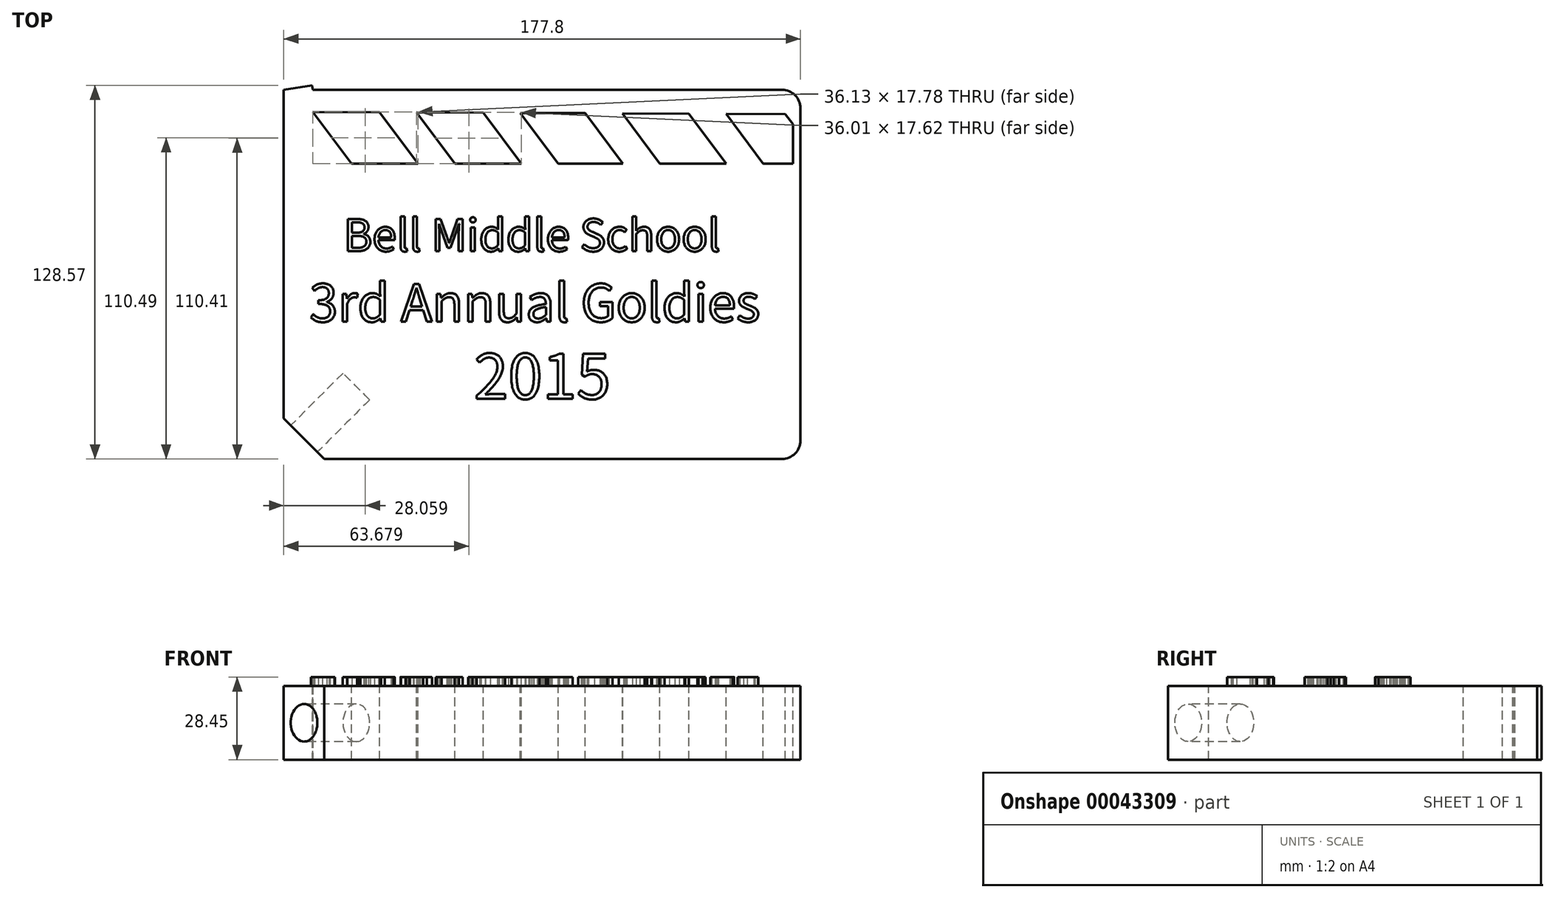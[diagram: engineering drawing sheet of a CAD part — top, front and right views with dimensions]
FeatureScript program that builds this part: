
annotation { "Feature Type Name" : "Feature", "Feature Type Description" : "" }
export const myFeature = defineFeature(function(context is Context, id is Id, definition is map)
    precondition{}
    {
        {
            var Q0;
            Q0=qCreatedBy(makeId("Top.planeOp"),FACE);
            var sketch = newSketch(context, id + "F0", { "sketchPlane" : qUnion([Q0])});
            skLineSegment(sketch, "E0.bottom", {"start": v(-85.65, 77.21) * mm, "end": v(85.8, 77.21) * mm});
            skLineSegment(sketch, "E0.top", {"start": v(-79.3, -49.79) * mm, "end": v(85.8, -49.79) * mm});
            skLineSegment(sketch, "E0.left", {"start": v(-85.65, 77.21) * mm, "end": v(-85.65, -43.44) * mm});
            skLineSegment(sketch, "E0.right", {"start": v(92.15, 70.86) * mm, "end": v(92.15, -43.44) * mm});
            skLineSegment(sketch, "E1", {"start": v(-85.65, 77.21) * mm, "end": v(-108.44, 107.74) * mm});
            skLineSegment(sketch, "E2", {"start": v(-102.2, 99.38) * mm, "end": v(-85.65, 77.21) * mm});
            skLineSegment(sketch, "E3", {"start": v(-85.65, 77.21) * mm, "end": v(79.18, 103.64) * mm});
            skLineSegment(sketch, "E4", {"start": v(83.36, 113.58) * mm, "end": v(69.28, 133.5) * mm});
            skLineSegment(sketch, "E5", {"start": v(63.05, 136.1) * mm, "end": v(-98.15, 109.45) * mm});
            skPoint(sketch, "E6.visualSharp", {"position": v(-108.44, 107.74) * mm});
            skArc(sketch, "E6.filletArc", {"start": v(-98.15, 109.45) * mm, "mid": v(-103, 105.55) * mm, "end": v(-102.2, 99.38) * mm});
            skPoint(sketch, "E7.visualSharp", {"position": v(66.98, 136.75) * mm});
            skArc(sketch, "E7.filletArc", {"start": v(69.28, 133.5) * mm, "mid": v(66.54, 135.7) * mm, "end": v(63.05, 136.1) * mm});
            skPoint(sketch, "E8.visualSharp", {"position": v(89.24, 105.25) * mm});
            skArc(sketch, "E8.filletArc", {"start": v(79.18, 103.64) * mm, "mid": v(84.02, 107.45) * mm, "end": v(83.36, 113.58) * mm});
            skPoint(sketch, "E9.visualSharp", {"position": v(92.15, 77.21) * mm});
            skArc(sketch, "E9.filletArc", {"start": v(92.15, 70.86) * mm, "mid": v(90.3, 75.35) * mm, "end": v(85.8, 77.21) * mm});
            skPoint(sketch, "E10.visualSharp", {"position": v(-85.65, -49.79) * mm});
            skArc(sketch, "E10.filletArc", {"start": v(-85.65, -43.44) * mm, "mid": v(-83.79, -47.93) * mm, "end": v(-79.3, -49.79) * mm});
            skPoint(sketch, "E11.visualSharp", {"position": v(92.15, -49.79) * mm});
            skArc(sketch, "E11.filletArc", {"start": v(85.8, -49.79) * mm, "mid": v(90.3, -47.93) * mm, "end": v(92.15, -43.44) * mm});
            skLineSegment(sketch, "E12", {"start": v(70.72, 131.46) * mm, "end": v(83.36, 113.58) * mm});
            skLineSegment(sketch, "E13", {"start": v(-91.83, 85.48) * mm, "end": v(-85.65, 77.21) * mm});
            skLineSegment(sketch, "E14", {"start": v(-74.04, 105.7) * mm, "end": v(-60.84, 88.03) * mm});
            skLineSegment(sketch, "E15", {"start": v(-48.3, 90.04) * mm, "end": v(-61.54, 107.77) * mm});
            skLineSegment(sketch, "E16", {"start": v(-61.54, 107.77) * mm, "end": v(-39.05, 111.5) * mm});
            skLineSegment(sketch, "E17", {"start": v(-39.05, 111.5) * mm, "end": v(-25.73, 93.66) * mm});
            skLineSegment(sketch, "E18", {"start": v(-25.73, 93.66) * mm, "end": v(-25.44, 93.7) * mm});
            skLineSegment(sketch, "E19", {"start": v(-25.44, 93.7) * mm, "end": v(-38.76, 111.54) * mm});
            skLineSegment(sketch, "E20", {"start": v(-27.03, 113.48) * mm, "end": v(-13.67, 95.59) * mm});
            skLineSegment(sketch, "E21", {"start": v(-13.67, 95.59) * mm, "end": v(9.19, 99.25) * mm});
            skLineSegment(sketch, "E22", {"start": v(9.19, 99.25) * mm, "end": v(-4.24, 117.25) * mm});
            skLineSegment(sketch, "E23", {"start": v(8.41, 119.34) * mm, "end": v(21.89, 101.3) * mm});
            skLineSegment(sketch, "E24", {"start": v(21.89, 101.3) * mm, "end": v(44.75, 104.96) * mm});
            skLineSegment(sketch, "E25", {"start": v(44.75, 104.96) * mm, "end": v(31.2, 123.1) * mm});
            skLineSegment(sketch, "E26", {"start": v(43.86, 125.2) * mm, "end": v(57.45, 107) * mm});
            skLineSegment(sketch, "E27", {"start": v(57.45, 107) * mm, "end": v(80.02, 110.61) * mm});
            skLineSegment(sketch, "E28", {"start": v(80.02, 110.61) * mm, "end": v(66.35, 128.92) * mm});
            skLineSegment(sketch, "E29", {"start": v(-74.04, 105.7) * mm, "end": v(-96.9, 101.93) * mm});
            skLineSegment(sketch, "E30", {"start": v(-27.03, 113.48) * mm, "end": v(-4.24, 117.25) * mm});
            skLineSegment(sketch, "E31", {"start": v(8.41, 119.34) * mm, "end": v(31.2, 123.1) * mm});
            skLineSegment(sketch, "E32", {"start": v(43.86, 125.2) * mm, "end": v(66.35, 128.92) * mm});
            skLineSegment(sketch, "E33", {"start": v(-25.44, 93.7) * mm, "end": v(-48.3, 90.04) * mm});
            skLineSegment(sketch, "E34", {"start": v(-60.84, 88.03) * mm, "end": v(-83.78, 84.35) * mm});
            skLineSegment(sketch, "E35", {"start": v(-96.9, 101.93) * mm, "end": v(-83.78, 84.35) * mm});
            skLineSegment(sketch, "E36", {"start": v(-75.87, 78.78) * mm, "end": v(-75.62, 77.21) * mm});
            skSolve(sketch);
        }
        {
            var Q0;
            {var subQ1=sQuery(id+"F0.wireOp",EDGE,"E36");Q0=makeQuery(id+"F0.imprint","IMPRINT",FACE,{"disambiguationData":[TD([[makeQuery(id+"F0.imprint","IMPRINT",EDGE,{"derivedFrom":subQ1}),-1.0]])]});}
            var Q1;
            Q1=makeQuery(id+"F0.imprint","IMPRINT",FACE,{"disambiguationData":[TD([[makeQuery(id+"F0.imprint","IMPRINT",EDGE,{"derivedFrom":sQuery(id+"F0.wireOp",EDGE,"E2")}),1.0]])]});
            var Q2;
            Q2=makeQuery(id+"F0.imprint","IMPRINT",FACE,{"disambiguationData":[TD([[makeQuery(id+"F0.imprint","IMPRINT",EDGE,{"derivedFrom":sQuery(id+"F0.wireOp",EDGE,"E0.top")}),1.0]])]});
            extrude(context, id + "F1", {"entities" : qUnion([Q0, Q1, Q2]), "depth" : 25.4 * mm});
        }
        {
            var Q0;
            Q0=makeQuery(id+"F1.opExtrude","CAP_FACE",FACE,{"disambiguationData":[OSD([sQuery(id+"F0.wireOp",EDGE,"E0.bottom"),sQuery(id+"F0.wireOp",EDGE,"E0.top"),sQuery(id+"F0.wireOp",EDGE,"E0.left"),sQuery(id+"F0.wireOp",EDGE,"E0.right"),sQuery(id+"F0.wireOp",EDGE,"E2"),sQuery(id+"F0.wireOp",EDGE,"E3"),sQuery(id+"F0.wireOp",EDGE,"E4"),sQuery(id+"F0.wireOp",EDGE,"E5"),sQuery(id+"F0.wireOp",EDGE,"E6.filletArc"),sQuery(id+"F0.wireOp",EDGE,"E7.filletArc"),sQuery(id+"F0.wireOp",EDGE,"E8.filletArc"),sQuery(id+"F0.wireOp",EDGE,"E9.filletArc"),sQuery(id+"F0.wireOp",EDGE,"E10.filletArc"),sQuery(id+"F0.wireOp",EDGE,"E11.filletArc"),sQuery(id+"F0.wireOp",EDGE,"E12"),sQuery(id+"F0.wireOp",EDGE,"E13"),sQuery(id+"F0.wireOp",EDGE,"E14"),sQuery(id+"F0.wireOp",EDGE,"E15"),sQuery(id+"F0.wireOp",EDGE,"E16"),sQuery(id+"F0.wireOp",EDGE,"E17"),sQuery(id+"F0.wireOp",EDGE,"E20"),sQuery(id+"F0.wireOp",EDGE,"E21"),sQuery(id+"F0.wireOp",EDGE,"E22"),sQuery(id+"F0.wireOp",EDGE,"E23"),sQuery(id+"F0.wireOp",EDGE,"E24"),sQuery(id+"F0.wireOp",EDGE,"E25"),sQuery(id+"F0.wireOp",EDGE,"E26"),sQuery(id+"F0.wireOp",EDGE,"E27"),sQuery(id+"F0.wireOp",EDGE,"E28"),sQuery(id+"F0.wireOp",EDGE,"E29"),sQuery(id+"F0.wireOp",EDGE,"E30"),sQuery(id+"F0.wireOp",EDGE,"E31"),sQuery(id+"F0.wireOp",EDGE,"E32"),sQuery(id+"F0.wireOp",EDGE,"E33"),sQuery(id+"F0.wireOp",EDGE,"E34"),sQuery(id+"F0.wireOp",EDGE,"E35"),sQuery(id+"F0.wireOp",EDGE,"E36")])],"isStart":false});
            var sketch = newSketch(context, id + "F2", { "sketchPlane" : qUnion([Q0])});
            skPoint(sketch, "E37.endSnap0", {"position": v(-75.74, 78) * mm});
            skLineSegment(sketch, "E38", {"start": v(-75.66, 69.6) * mm, "end": v(-62.39, 51.81) * mm});
            skLineSegment(sketch, "E39", {"start": v(-62.39, 51.81) * mm, "end": v(-39.53, 51.81) * mm});
            skLineSegment(sketch, "E40", {"start": v(-39.53, 51.81) * mm, "end": v(-52.72, 69.49) * mm});
            skLineSegment(sketch, "E41", {"start": v(-39.98, 69.43) * mm, "end": v(-26.83, 51.81) * mm});
            skLineSegment(sketch, "E42", {"start": v(-26.83, 51.81) * mm, "end": v(-3.97, 51.81) * mm});
            skLineSegment(sketch, "E43", {"start": v(-3.97, 51.81) * mm, "end": v(-17.04, 69.33) * mm});
            skLineSegment(sketch, "E44", {"start": v(-4.3, 69.27) * mm, "end": v(8.73, 51.81) * mm});
            skPoint(sketch, "E44.endSnap0", {"position": v(8.2, 51.81) * mm});
            skLineSegment(sketch, "E45", {"start": v(8.73, 51.81) * mm, "end": v(31.06, 51.81) * mm});
            skLineSegment(sketch, "E46", {"start": v(31.06, 51.81) * mm, "end": v(18.1, 69.17) * mm});
            skLineSegment(sketch, "E47", {"start": v(30.85, 69.1) * mm, "end": v(43.76, 51.81) * mm});
            skLineSegment(sketch, "E48", {"start": v(43.76, 51.81) * mm, "end": v(66.62, 51.81) * mm});
            skLineSegment(sketch, "E49", {"start": v(66.62, 51.81) * mm, "end": v(53.79, 69) * mm});
            skLineSegment(sketch, "E50", {"start": v(53.79, 69) * mm, "end": v(54.21, 69) * mm});
            skLineSegment(sketch, "E51", {"start": v(54.21, 69) * mm, "end": v(67.05, 51.81) * mm});
            skLineSegment(sketch, "E52", {"start": v(79.32, 51.81) * mm, "end": v(66.53, 68.95) * mm});
            skLineSegment(sketch, "E53", {"start": v(86.94, 68.86) * mm, "end": v(92.15, 61.88) * mm});
            skLineSegment(sketch, "E54", {"start": v(79.32, 51.81) * mm, "end": v(92.15, 51.81) * mm});
            skLineSegment(sketch, "E55", {"start": v(92.15, 51.81) * mm, "end": v(92.15, 61.88) * mm});
            skLineSegment(sketch, "E56", {"start": v(66.53, 68.95) * mm, "end": v(86.94, 68.86) * mm});
            skLineSegment(sketch, "E57", {"start": v(54.21, 69) * mm, "end": v(30.85, 69.1) * mm});
            skLineSegment(sketch, "E58", {"start": v(18.1, 69.17) * mm, "end": v(-4.3, 69.27) * mm});
            skLineSegment(sketch, "E59", {"start": v(-17.04, 69.33) * mm, "end": v(-39.98, 69.43) * mm});
            skLineSegment(sketch, "E60", {"start": v(-52.72, 69.49) * mm, "end": v(-75.66, 69.6) * mm});
            skLineSegment(sketch, "E61", {"start": v(89.55, 65.37) * mm, "end": v(89.55, 51.81) * mm});
            skSolve(sketch);
        }
        {
            var Q0;
            Q0=makeQuery(id+"F2.imprint","IMPRINT",FACE,{"disambiguationData":[TD([[makeQuery(id+"F2.imprint","IMPRINT",EDGE,{"derivedFrom":sQuery(id+"F2.wireOp",EDGE,"E38")}),1.0]])]});
            var Q1;
            Q1=makeQuery(id+"F2.imprint","IMPRINT",FACE,{"disambiguationData":[TD([[makeQuery(id+"F2.imprint","IMPRINT",EDGE,{"derivedFrom":sQuery(id+"F2.wireOp",EDGE,"E41")}),1.0]])]});
            var Q2;
            Q2=makeQuery(id+"F2.imprint","IMPRINT",FACE,{"disambiguationData":[TD([[makeQuery(id+"F2.imprint","IMPRINT",EDGE,{"derivedFrom":sQuery(id+"F2.wireOp",EDGE,"E44")}),1.0]])]});
            var Q3;
            {var subQ2=sQuery(id+"F2.wireOp",EDGE,"E47");Q3=makeQuery(id+"F2.imprint","IMPRINT",FACE,{"disambiguationData":[TD([[makeQuery(id+"F2.imprint","IMPRINT",EDGE,{"derivedFrom":subQ2}),1.0]])]});}
            var Q4;
            Q4=makeQuery(id+"F2.imprint","IMPRINT",FACE,{"disambiguationData":[TD([[makeQuery(id+"F2.imprint","IMPRINT",EDGE,{"derivedFrom":sQuery(id+"F2.wireOp",EDGE,"E52")}),-1.0]])]});
            extrude(context, id + "F3", {"entities" : qUnion([Q0, Q1, Q2, Q3, Q4]), "operationType" : NewBodyOperationType.REMOVE, "endBound" : BoundingType.THROUGH_ALL, "oppositeDirection" : true, "depth" : 25.4 * mm});
        }
        {
            var Q0;
            Q0=makeQuery(id+"F1.opExtrude","CAP_FACE",FACE,{"disambiguationData":[OSD([sQuery(id+"F0.wireOp",EDGE,"E0.bottom"),sQuery(id+"F0.wireOp",EDGE,"E0.top"),sQuery(id+"F0.wireOp",EDGE,"E0.left"),sQuery(id+"F0.wireOp",EDGE,"E0.right"),sQuery(id+"F0.wireOp",EDGE,"E2"),sQuery(id+"F0.wireOp",EDGE,"E3"),sQuery(id+"F0.wireOp",EDGE,"E4"),sQuery(id+"F0.wireOp",EDGE,"E5"),sQuery(id+"F0.wireOp",EDGE,"E6.filletArc"),sQuery(id+"F0.wireOp",EDGE,"E7.filletArc"),sQuery(id+"F0.wireOp",EDGE,"E8.filletArc"),sQuery(id+"F0.wireOp",EDGE,"E9.filletArc"),sQuery(id+"F0.wireOp",EDGE,"E10.filletArc"),sQuery(id+"F0.wireOp",EDGE,"E11.filletArc"),sQuery(id+"F0.wireOp",EDGE,"E12"),sQuery(id+"F0.wireOp",EDGE,"E13"),sQuery(id+"F0.wireOp",EDGE,"E14"),sQuery(id+"F0.wireOp",EDGE,"E15"),sQuery(id+"F0.wireOp",EDGE,"E16"),sQuery(id+"F0.wireOp",EDGE,"E17"),sQuery(id+"F0.wireOp",EDGE,"E20"),sQuery(id+"F0.wireOp",EDGE,"E21"),sQuery(id+"F0.wireOp",EDGE,"E22"),sQuery(id+"F0.wireOp",EDGE,"E23"),sQuery(id+"F0.wireOp",EDGE,"E24"),sQuery(id+"F0.wireOp",EDGE,"E25"),sQuery(id+"F0.wireOp",EDGE,"E26"),sQuery(id+"F0.wireOp",EDGE,"E27"),sQuery(id+"F0.wireOp",EDGE,"E28"),sQuery(id+"F0.wireOp",EDGE,"E29"),sQuery(id+"F0.wireOp",EDGE,"E30"),sQuery(id+"F0.wireOp",EDGE,"E31"),sQuery(id+"F0.wireOp",EDGE,"E32"),sQuery(id+"F0.wireOp",EDGE,"E33"),sQuery(id+"F0.wireOp",EDGE,"E34"),sQuery(id+"F0.wireOp",EDGE,"E35"),sQuery(id+"F0.wireOp",EDGE,"E36")])],"isStart":false});
            var sketch = newSketch(context, id + "F4", { "sketchPlane" : qUnion([Q0])});
            skText(sketch, "E62", { "text": "Bell Middle School", "fontName": "NotoSansCJKjp-Regular.otf"});
            skText(sketch, "E63", { "text": "3rd Annual Goldies", "fontName": "NotoSansCJKjp-Regular.otf"});
            skText(sketch, "E64", { "text": "2015", "fontName": "NotoSansCJKjp-Regular.otf"});
            const initialGuessF4  = {"E62": [-0.0651, 0.02171, 1, 0, 0.01085], "E63": [-0.07686, -0.00254, 1, 0, 0.0127], "E64": [-0.02019, -0.02912, 1, 0, 0.01524]};
            skSetInitialGuess(sketch, initialGuessF4);
            skSolve(sketch);
        }
        {
            var Q0;
            Q0 = qSketchRegion(id + "F4", true);
            extrude(context, id + "F5", {"entities" : qUnion([Q0]), "operationType" : NewBodyOperationType.ADD, "depth" : 3.05 * mm});
        }
        {
            var Q0;
            {var subQ0=sQuery(id+"F0.wireOp",EDGE,"E0.bottom");var subQ1=sQuery(id+"F0.wireOp",EDGE,"E0.top");var subQ2=sQuery(id+"F0.wireOp",EDGE,"E0.left");var subQ3=sQuery(id+"F0.wireOp",EDGE,"E0.right");var subQ4=sQuery(id+"F0.wireOp",EDGE,"E2");var subQ5=sQuery(id+"F0.wireOp",EDGE,"E3");var subQ6=sQuery(id+"F0.wireOp",EDGE,"E4");var subQ7=sQuery(id+"F0.wireOp",EDGE,"E5");var subQ8=sQuery(id+"F0.wireOp",EDGE,"E6.filletArc");var subQ9=sQuery(id+"F0.wireOp",EDGE,"E7.filletArc");var subQ10=sQuery(id+"F0.wireOp",EDGE,"E8.filletArc");var subQ11=sQuery(id+"F0.wireOp",EDGE,"E9.filletArc");var subQ12=sQuery(id+"F0.wireOp",EDGE,"E10.filletArc");var subQ13=sQuery(id+"F0.wireOp",EDGE,"E11.filletArc");var subQ14=sQuery(id+"F0.wireOp",EDGE,"E12");var subQ15=sQuery(id+"F0.wireOp",EDGE,"E13");var subQ16=sQuery(id+"F0.wireOp",EDGE,"E14");var subQ17=sQuery(id+"F0.wireOp",EDGE,"E15");var subQ18=sQuery(id+"F0.wireOp",EDGE,"E16");var subQ19=sQuery(id+"F0.wireOp",EDGE,"E17");var subQ20=sQuery(id+"F0.wireOp",EDGE,"E20");var subQ21=sQuery(id+"F0.wireOp",EDGE,"E21");var subQ22=sQuery(id+"F0.wireOp",EDGE,"E22");var subQ23=sQuery(id+"F0.wireOp",EDGE,"E23");var subQ24=sQuery(id+"F0.wireOp",EDGE,"E24");var subQ25=sQuery(id+"F0.wireOp",EDGE,"E25");var subQ26=sQuery(id+"F0.wireOp",EDGE,"E26");var subQ27=sQuery(id+"F0.wireOp",EDGE,"E27");var subQ28=sQuery(id+"F0.wireOp",EDGE,"E28");var subQ29=sQuery(id+"F0.wireOp",EDGE,"E29");var subQ30=sQuery(id+"F0.wireOp",EDGE,"E30");var subQ31=sQuery(id+"F0.wireOp",EDGE,"E31");var subQ32=sQuery(id+"F0.wireOp",EDGE,"E32");var subQ33=sQuery(id+"F0.wireOp",EDGE,"E33");var subQ34=sQuery(id+"F0.wireOp",EDGE,"E34");var subQ35=sQuery(id+"F0.wireOp",EDGE,"E35");var subQ36=sQuery(id+"F0.wireOp",EDGE,"E36");Q0=makeQuery(id+"F5.boolean.opBoolean","SPLIT",FACE,{"disambiguationData":[TD([makeQuery(id+"F1.opExtrude","SWEPT_FACE",FACE,{"disambiguationData":[OSD([subQ0])]})])],"derivedFrom":makeQuery(id+"F1.opExtrude","CAP_FACE",FACE,{"disambiguationData":[OSD([subQ0,subQ1,subQ2,subQ3,subQ4,subQ5,subQ6,subQ7,subQ8,subQ9,subQ10,subQ11,subQ12,subQ13,subQ14,subQ15,subQ16,subQ17,subQ18,subQ19,subQ20,subQ21,subQ22,subQ23,subQ24,subQ25,subQ26,subQ27,subQ28,subQ29,subQ30,subQ31,subQ32,subQ33,subQ34,subQ35,subQ36])],"isStart":false})});}
            var sketch = newSketch(context, id + "F6", { "sketchPlane" : qUnion([Q0])});
            skLineSegment(sketch, "E65", {"start": v(-85.65, -35.82) * mm, "end": v(-71.68, -49.79) * mm});
            skSolve(sketch);
        }
        {
            var Q0;
            {var subQ1=sQuery(id+"F6.wireOp",EDGE,"E65");Q0=makeQuery(id+"F6.imprint","IMPRINT",FACE,{"disambiguationData":[TD([[makeQuery(id+"F6.imprint","IMPRINT",EDGE,{"derivedFrom":subQ1}),-1.0]])]});}
            extrude(context, id + "F7", {"entities" : qUnion([Q0]), "operationType" : NewBodyOperationType.REMOVE, "endBound" : BoundingType.THROUGH_ALL, "oppositeDirection" : true, "depth" : 25.4 * mm});
        }
        {
            var Q0;
            Q0=makeQuery(id+"F7.boolean.opBoolean","COPY",FACE,{"derivedFrom":makeQuery(id+"F7.opExtrude","SWEPT_FACE",FACE,{"disambiguationData":[OSD([sQuery(id+"F6.wireOp",EDGE,"E65")])]})});
            var sketch = newSketch(context, id + "F8", { "sketchPlane" : qUnion([Q0])});
            skCircle(sketch, "E66", {"center": v(-25.36, 12.7) * mm, "radius": 6.48 * mm});
            skSolve(sketch);
        }
        {
            var Q0;
            Q0=makeQuery(id+"F8.imprint","IMPRINT",FACE,{"disambiguationData":[TD([[makeQuery(id+"F8.imprint","IMPRINT",EDGE,{"derivedFrom":sQuery(id+"F8.wireOp",EDGE,"E66")}),1.0]])]});
            extrude(context, id + "F9", {"entities" : qUnion([Q0]), "operationType" : NewBodyOperationType.REMOVE, "oppositeDirection" : true, "depth" : 25.4 * mm});
        }
    });
